# Revit family: 306_fc925d7a4491461b9c782ec4008454
name_source: partatom
category: Pipe Accessories
units: mm (PartAtom-declared; Revit-internal decimal feet)

## family parameters
Always vertical = Yes
Cut with Voids When Loaded = No
Part Type = Valve - Breaks Into
Round Connector Dimension = Use Diameter
Shared = No
Work Plane-Based = No

## types (8) — shared parameters
Description = 2-way Control valve VLA325, PN16 flange
L2D_Min = 3048 mm
Manufacturer = ESBE
QmdConnectorList = 301;D;302;D
R9 = 4 mm  [stored 0.0131234 ft]
URL = http://www.esbe.eu
X1 = 2 mm  [stored 0.00656168 ft]
Z10 = 2 mm  [stored 0.00656168 ft]
Z4 = 17 mm  [stored 0.0557743 ft]
Z7 = 3 mm  [stored 0.00984252 ft]
Z8 = 13 mm
Z9 = 4 mm  [stored 0.0131234 ft]
magiPartTypeId = 306
magiProductFamilyId = fc925d7a4491461b9c782ec4008454

## per-type parameters (varying)
- VLA325 PN16 FLANGE DN15-1,6: CenSd_R6_6=10 mm  [stored 0.0328084 ft]; D=15 mm; D2=25 mm  [stored 0.082021 ft]; D3=26 mm; D4=22 mm  [stored 0.0721785 ft]; FDT2=48 mm; H3=38 mm; H4=42 mm; HCDT2=22 mm  [stored 0.0721785 ft]; L2D=130 mm; LT2=65 mm; R1=13 mm; R2=17 mm  [stored 0.0557743 ft]; R3=22 mm  [stored 0.0721785 ft]; R4=18 mm; R5=14 mm  [stored 0.0459318 ft]; R6=12 mm  [stored 0.0393701 ft]; R7=7 mm  [stored 0.0229659 ft]; R8=5 mm  [stored 0.0164042 ft]; W2D=15 mm  [stored 0.0492126 ft]; X2=6 mm  [stored 0.019685 ft]; X2__ve=-6 mm; Z12=11 mm; Z12__ve=-11 mm  [stored -0.0360892 ft]; Z13=5 mm  [stored 0.0164042 ft]; Z14=5 mm  [stored 0.0164042 ft]; Z14__ve=-5 mm  [stored -0.0164042 ft]; Z15=13 mm; Z3=55 mm; Z5=9 mm  [stored 0.0295276 ft]; Z6=9 mm  [stored 0.0295276 ft]; magiProductId=a9756149740e4e4499aa47cb77daf5
- VLA325 PN16 FLANGE DN50-38: CenSd_R6_6=18 mm; D=50 mm; D2=45 mm; D3=53 mm; D4=45 mm; FDT2=83 mm; H3=76 mm; H4=74 mm; HCDT2=48 mm; L2D=230 mm; LT2=115 mm; R1=29 mm; R2=36 mm; R3=39 mm; R4=31 mm; R5=25 mm  [stored 0.082021 ft]; R6=21 mm; R7=13 mm; R8=10 mm  [stored 0.0328084 ft]; W2D=50 mm; X2=11 mm; X2__ve=-11 mm  [stored -0.0360892 ft]; Z12=19 mm  [stored 0.062336 ft]; Z12__ve=-19 mm; Z13=9 mm  [stored 0.0295276 ft]; Z14=10 mm  [stored 0.0328084 ft]; Z14__ve=-10 mm  [stored -0.0328084 ft]; Z15=27 mm; Z3=103 mm; Z5=9 mm  [stored 0.0295276 ft]; Z6=9 mm  [stored 0.0295276 ft]; magiProductId=6f4fc29ca3e9446f925ee6f0760089
- VLA325 PN16 FLANGE DN40-25: CenSd_R6_6=16 mm; D=40 mm; D2=39 mm; D3=46 mm; D4=39 mm; FDT2=75 mm; H3=61 mm; H4=60 mm; HCDT2=41 mm; L2D=200 mm; LT2=100 mm; R1=24 mm; R2=31 mm; R3=34 mm; R4=27 mm; R5=22 mm  [stored 0.0721785 ft]; R6=18 mm; R7=11 mm; R8=8 mm  [stored 0.0262467 ft]; W2D=40 mm; X2=10 mm  [stored 0.0328084 ft]; X2__ve=-10 mm  [stored -0.0328084 ft]; Z12=15 mm  [stored 0.0492126 ft]; Z12__ve=-15 mm; Z13=8 mm  [stored 0.0262467 ft]; Z14=8 mm  [stored 0.0262467 ft]; Z14__ve=-8 mm; Z15=21 mm; Z3=83 mm; Z5=9 mm  [stored 0.0295276 ft]; Z6=9 mm  [stored 0.0295276 ft]; magiProductId=0bdf6d82c7964c4abe06221169341d
- VLA325 PN16 FLANGE DN32-16: CenSd_R6_6=14 mm  [stored 0.0459318 ft]; D=32 mm; D2=35 mm; D3=41 mm; D4=34 mm; FDT2=70 mm; H3=60 mm; H4=58 mm; HCDT2=36 mm; L2D=180 mm; LT2=90 mm; R1=21 mm; R2=27 mm; R3=31 mm; R4=24 mm; R5=20 mm  [stored 0.0656168 ft]; R6=17 mm  [stored 0.0557743 ft]; R7=10 mm  [stored 0.0328084 ft]; R8=7 mm  [stored 0.0229659 ft]; W2D=32 mm; X2=9 mm  [stored 0.0295276 ft]; X2__ve=-9 mm; Z12=15 mm  [stored 0.0492126 ft]; Z12__ve=-15 mm; Z13=7 mm  [stored 0.0229659 ft]; Z14=8 mm  [stored 0.0262467 ft]; Z14__ve=-8 mm; Z15=21 mm; Z3=81 mm; Z5=8 mm  [stored 0.0262467 ft]; Z6=8 mm  [stored 0.0262467 ft]; magiProductId=ee8f3cd8af364824a2a07b4428f488
- VLA325 PN16 FLANGE DN25-10: CenSd_R6_6=13 mm; D=25 mm; D2=31 mm; D3=36 mm; D4=30 mm  [stored 0.0984252 ft]; FDT2=58 mm; H3=46 mm; H4=44 mm; HCDT2=32 mm; L2D=160 mm; LT2=80 mm; R1=19 mm  [stored 0.062336 ft]; R2=24 mm; R3=27 mm; R4=22 mm  [stored 0.0721785 ft]; R5=17 mm  [stored 0.0557743 ft]; R6=15 mm  [stored 0.0492126 ft]; R7=9 mm  [stored 0.0295276 ft]; R8=7 mm  [stored 0.0229659 ft]; W2D=25 mm  [stored 0.082021 ft]; X2=8 mm  [stored 0.0262467 ft]; X2__ve=-8 mm; Z12=11 mm; Z12__ve=-11 mm  [stored -0.0360892 ft]; Z13=6 mm  [stored 0.019685 ft]; Z14=6 mm  [stored 0.019685 ft]; Z14__ve=-6 mm; Z15=16 mm; Z3=62 mm; Z5=9 mm  [stored 0.0295276 ft]; Z6=9 mm  [stored 0.0295276 ft]; magiProductId=1c843dd1c0934541a72d51b03b179a
- VLA325 PN16 FLANGE DN20-6,3: CenSd_R6_6=12 mm  [stored 0.0393701 ft]; D=20 mm; D2=29 mm; D3=31 mm; D4=26 mm; FDT2=53 mm; H3=41 mm; H4=44 mm; HCDT2=27 mm; L2D=150 mm; LT2=75 mm; R1=16 mm; R2=20 mm  [stored 0.0656168 ft]; R3=25 mm  [stored 0.082021 ft]; R4=20 mm  [stored 0.0656168 ft]; R5=16 mm; R6=14 mm  [stored 0.0459318 ft]; R7=8 mm  [stored 0.0262467 ft]; R8=6 mm  [stored 0.019685 ft]; W2D=20 mm  [stored 0.0656168 ft]; X2=7 mm  [stored 0.0229659 ft]; X2__ve=-7 mm; Z12=11 mm; Z12__ve=-11 mm  [stored -0.0360892 ft]; Z13=6 mm  [stored 0.019685 ft]; Z14=5 mm  [stored 0.0164042 ft]; Z14__ve=-5 mm  [stored -0.0164042 ft]; Z15=14 mm  [stored 0.0459318 ft]; Z3=58 mm; Z5=9 mm  [stored 0.0295276 ft]; Z6=9 mm  [stored 0.0295276 ft]; magiProductId=333091fc85b34b618b859c28e0620a
- VLA325 PN16 FLANGE DN15-4,0: CenSd_R6_6=10 mm  [stored 0.0328084 ft]; D=15 mm; D2=25 mm  [stored 0.082021 ft]; D3=26 mm; D4=22 mm  [stored 0.0721785 ft]; FDT2=48 mm; H3=38 mm; H4=42 mm; HCDT2=22 mm  [stored 0.0721785 ft]; L2D=130 mm; LT2=65 mm; R1=13 mm; R2=17 mm  [stored 0.0557743 ft]; R3=22 mm  [stored 0.0721785 ft]; R4=18 mm; R5=14 mm  [stored 0.0459318 ft]; R6=12 mm  [stored 0.0393701 ft]; R7=7 mm  [stored 0.0229659 ft]; R8=5 mm  [stored 0.0164042 ft]; W2D=15 mm  [stored 0.0492126 ft]; X2=6 mm  [stored 0.019685 ft]; X2__ve=-6 mm; Z12=11 mm; Z12__ve=-11 mm  [stored -0.0360892 ft]; Z13=5 mm  [stored 0.0164042 ft]; Z14=5 mm  [stored 0.0164042 ft]; Z14__ve=-5 mm  [stored -0.0164042 ft]; Z15=13 mm; Z3=55 mm; Z5=9 mm  [stored 0.0295276 ft]; Z6=9 mm  [stored 0.0295276 ft]; magiProductId=a42047a7a803471ab91d038e8ea8ad
- VLA325 PN16 FLANGE DN15-2,5: CenSd_R6_6=10 mm  [stored 0.0328084 ft]; D=15 mm; D2=25 mm  [stored 0.082021 ft]; D3=26 mm; D4=22 mm  [stored 0.0721785 ft]; FDT2=48 mm; H3=38 mm; H4=42 mm; HCDT2=22 mm  [stored 0.0721785 ft]; L2D=130 mm; LT2=65 mm; R1=13 mm; R2=17 mm  [stored 0.0557743 ft]; R3=22 mm  [stored 0.0721785 ft]; R4=18 mm; R5=14 mm  [stored 0.0459318 ft]; R6=12 mm  [stored 0.0393701 ft]; R7=7 mm  [stored 0.0229659 ft]; R8=5 mm  [stored 0.0164042 ft]; W2D=15 mm  [stored 0.0492126 ft]; X2=6 mm  [stored 0.019685 ft]; X2__ve=-6 mm; Z12=11 mm; Z12__ve=-11 mm  [stored -0.0360892 ft]; Z13=5 mm  [stored 0.0164042 ft]; Z14=5 mm  [stored 0.0164042 ft]; Z14__ve=-5 mm  [stored -0.0164042 ft]; Z15=13 mm; Z3=55 mm; Z5=9 mm  [stored 0.0295276 ft]; Z6=9 mm  [stored 0.0295276 ft]; magiProductId=7950927f77db4b2bb2260c6a892b4b

note: column(s) folded — value = type name in every type: magiProductCode

note: [stored X ft] marks values corroborated as IEEE doubles in the binary element streams (Revit-internal decimal feet)

## geometry (parser evidence)
native form markers: Sweep x2
no freeform markers — native parametric forms only
